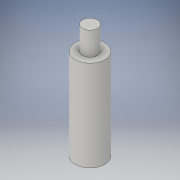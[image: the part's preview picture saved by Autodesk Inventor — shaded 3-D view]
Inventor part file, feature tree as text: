
AUTODESK INVENTOR PART (.ipt)
format: ipt  version: 2019 (Build 230136000, 136)  size: 100,864 bytes
history: native  units: in
note: dims shown in document units (in); Inventor stores cm internally (conversion verified against a paired STEP export)
features: extrude x2, sketch x2, projected_geometry x1
ambient origin geometry x8: Origin, YZ Plane, XZ Plane, XY Plane, X Axis, Y Axis, Z Axis, Center Point
bodies: Solid1 (feature_tree)
feature tree (5):
  extrude  "Extrusion1"  Depth=7.874in TaperAngle=0.0deg
  extrude  "Extrusion2"  Depth=1.6142in TaperAngle=0.0deg
  sketch  "Sketch1"  dims[d0=2.0472in d1=7.874in d2=0.0in]
  sketch  "Sketch2"  dims[d3=1.0236in d4=1.6142in d5=0.0in]
  projected_geometry  "Projected Loop1"
